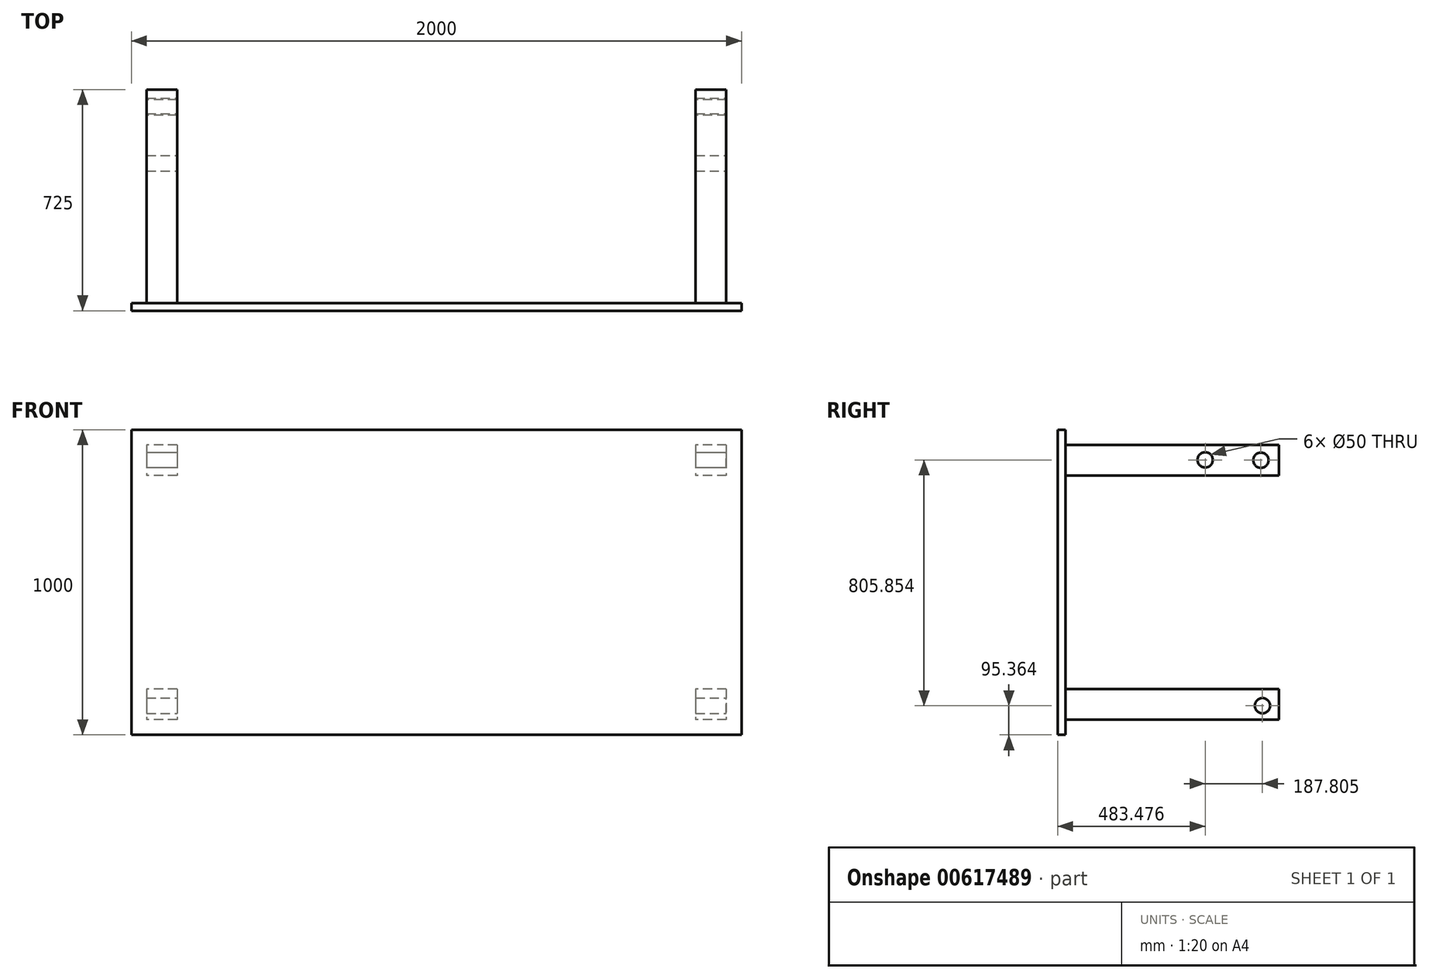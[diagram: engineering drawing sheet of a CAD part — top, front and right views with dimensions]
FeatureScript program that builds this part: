
annotation { "Feature Type Name" : "Feature", "Feature Type Description" : "" }
export const myFeature = defineFeature(function(context is Context, id is Id, definition is map)
    precondition{}
    {
        {
            var Q0;
            Q0=qCreatedBy(makeId("Front.planeOp"),FACE);
            var sketch = newSketch(context, id + "F0", { "sketchPlane" : qUnion([Q0])});
            skLineSegment(sketch, "E0.bottom", {"start": v(-997.25, 771.34) * mm, "end": v(1002.75, 771.34) * mm});
            skLineSegment(sketch, "E0.top", {"start": v(-997.25, -228.66) * mm, "end": v(1002.75, -228.66) * mm});
            skLineSegment(sketch, "E0.left", {"start": v(-997.25, 771.34) * mm, "end": v(-997.25, -228.66) * mm});
            skLineSegment(sketch, "E0.right", {"start": v(1002.75, 771.34) * mm, "end": v(1002.75, -228.66) * mm});
            skSolve(sketch);
        }
        {
            var Q0;
            Q0=makeQuery(id+"F0.imprint","IMPRINT",FACE,{"disambiguationData":[TD([[makeQuery(id+"F0.imprint","IMPRINT",EDGE,{"derivedFrom":sQuery(id+"F0.wireOp",EDGE,"E0.bottom")}),-1.0]])]});
            extrude(context, id + "F1", {"entities" : qUnion([Q0]), "depth" : 25 * mm, "offsetDistance" : 25 * mm});
        }
        {
            var Q0;
            Q0=makeQuery(id+"F1.opExtrude","CAP_FACE",FACE,{"disambiguationData":[OSD([sQuery(id+"F0.wireOp",EDGE,"E0.bottom"),sQuery(id+"F0.wireOp",EDGE,"E0.top"),sQuery(id+"F0.wireOp",EDGE,"E0.left"),sQuery(id+"F0.wireOp",EDGE,"E0.right")])],"isStart":true});
            var sketch = newSketch(context, id + "F2", { "sketchPlane" : qUnion([Q0])});
            skLineSegment(sketch, "E1.bottom", {"start": v(-952.75, 721.34) * mm, "end": v(-852.75, 721.34) * mm});
            skLineSegment(sketch, "E1.top", {"start": v(-952.75, 621.34) * mm, "end": v(-852.75, 621.34) * mm});
            skLineSegment(sketch, "E1.left", {"start": v(-952.75, 721.34) * mm, "end": v(-952.75, 621.34) * mm});
            skLineSegment(sketch, "E1.right", {"start": v(-852.75, 721.34) * mm, "end": v(-852.75, 621.34) * mm});
            skSolve(sketch);
        }
        {
            var Q0;
            Q0=makeQuery(id+"F2.imprint","IMPRINT",FACE,{"disambiguationData":[TD([[makeQuery(id+"F2.imprint","IMPRINT",EDGE,{"derivedFrom":sQuery(id+"F2.wireOp",EDGE,"E1.bottom")}),-1.0]])]});
            extrude(context, id + "F3", {"entities" : qUnion([Q0]), "operationType" : NewBodyOperationType.ADD, "depth" : 700 * mm, "offsetDistance" : 25 * mm});
        }
        {
            var Q0;
            Q0=makeQuery(id+"F1.opExtrude","CAP_FACE",FACE,{"disambiguationData":[OSD([sQuery(id+"F0.wireOp",EDGE,"E0.bottom"),sQuery(id+"F0.wireOp",EDGE,"E0.top"),sQuery(id+"F0.wireOp",EDGE,"E0.left"),sQuery(id+"F0.wireOp",EDGE,"E0.right")])],"isStart":true});
            var sketch = newSketch(context, id + "F4", { "sketchPlane" : qUnion([Q0])});
            skLineSegment(sketch, "E2.bottom", {"start": v(847.25, 721.34) * mm, "end": v(947.25, 721.34) * mm});
            skLineSegment(sketch, "E2.top", {"start": v(847.25, 621.34) * mm, "end": v(947.25, 621.34) * mm});
            skLineSegment(sketch, "E2.left", {"start": v(847.25, 721.34) * mm, "end": v(847.25, 621.34) * mm});
            skLineSegment(sketch, "E2.right", {"start": v(947.25, 721.34) * mm, "end": v(947.25, 621.34) * mm});
            skSolve(sketch);
        }
        {
            var Q0;
            Q0=makeQuery(id+"F4.imprint","IMPRINT",FACE,{"disambiguationData":[TD([[makeQuery(id+"F4.imprint","IMPRINT",EDGE,{"derivedFrom":sQuery(id+"F4.wireOp",EDGE,"E2.bottom")}),-1.0]])]});
            extrude(context, id + "F5", {"entities" : qUnion([Q0]), "operationType" : NewBodyOperationType.ADD, "depth" : 700 * mm, "offsetDistance" : 25 * mm});
        }
        {
            var Q0;
            Q0=makeQuery(id+"F1.opExtrude","CAP_FACE",FACE,{"disambiguationData":[OSD([sQuery(id+"F0.wireOp",EDGE,"E0.bottom"),sQuery(id+"F0.wireOp",EDGE,"E0.top"),sQuery(id+"F0.wireOp",EDGE,"E0.left"),sQuery(id+"F0.wireOp",EDGE,"E0.right")])],"isStart":true});
            var sketch = newSketch(context, id + "F6", { "sketchPlane" : qUnion([Q0])});
            skLineSegment(sketch, "E3.bottom", {"start": v(-952.75, -78.66) * mm, "end": v(-852.75, -78.66) * mm});
            skLineSegment(sketch, "E3.top", {"start": v(-952.75, -178.66) * mm, "end": v(-852.75, -178.66) * mm});
            skLineSegment(sketch, "E3.left", {"start": v(-952.75, -78.66) * mm, "end": v(-952.75, -178.66) * mm});
            skLineSegment(sketch, "E3.right", {"start": v(-852.75, -78.66) * mm, "end": v(-852.75, -178.66) * mm});
            skSolve(sketch);
        }
        {
            var Q0;
            Q0=makeQuery(id+"F6.imprint","IMPRINT",FACE,{"disambiguationData":[TD([[makeQuery(id+"F6.imprint","IMPRINT",EDGE,{"derivedFrom":sQuery(id+"F6.wireOp",EDGE,"E3.bottom")}),-1.0]])]});
            extrude(context, id + "F7", {"entities" : qUnion([Q0]), "operationType" : NewBodyOperationType.ADD, "depth" : 700 * mm, "offsetDistance" : 25 * mm});
        }
        {
            var Q0;
            Q0=makeQuery(id+"F1.opExtrude","CAP_FACE",FACE,{"disambiguationData":[OSD([sQuery(id+"F0.wireOp",EDGE,"E0.bottom"),sQuery(id+"F0.wireOp",EDGE,"E0.top"),sQuery(id+"F0.wireOp",EDGE,"E0.left"),sQuery(id+"F0.wireOp",EDGE,"E0.right")])],"isStart":true});
            var sketch = newSketch(context, id + "F8", { "sketchPlane" : qUnion([Q0])});
            skLineSegment(sketch, "E4.bottom", {"start": v(847.25, -78.66) * mm, "end": v(947.25, -78.66) * mm});
            skLineSegment(sketch, "E4.top", {"start": v(847.25, -178.66) * mm, "end": v(947.25, -178.66) * mm});
            skLineSegment(sketch, "E4.left", {"start": v(847.25, -78.66) * mm, "end": v(847.25, -178.66) * mm});
            skLineSegment(sketch, "E4.right", {"start": v(947.25, -78.66) * mm, "end": v(947.25, -178.66) * mm});
            skSolve(sketch);
        }
        {
            var Q0;
            Q0=makeQuery(id+"F8.imprint","IMPRINT",FACE,{"disambiguationData":[TD([[makeQuery(id+"F8.imprint","IMPRINT",EDGE,{"derivedFrom":sQuery(id+"F8.wireOp",EDGE,"E4.bottom")}),-1.0]])]});
            extrude(context, id + "F9", {"entities" : qUnion([Q0]), "operationType" : NewBodyOperationType.ADD, "depth" : 700 * mm, "offsetDistance" : 25 * mm});
        }
        {
            var Q0;
            Q0=makeQuery(id+"F5.opExtrude","SWEPT_FACE",FACE,{"disambiguationData":[OSD([sQuery(id+"F4.wireOp",EDGE,"E2.right")])]});
            var sketch = newSketch(context, id + "F10", { "sketchPlane" : qUnion([Q0])});
            skCircle(sketch, "E5", {"center": v(-641.16, 671.34) * mm, "radius": 25 * mm});
            skPoint(sketch, "E5.centerSnap0", {"position": v(-700, 671.34) * mm});
            skSolve(sketch);
        }
        {
            var Q0;
            Q0=makeQuery(id+"F10.imprint","IMPRINT",FACE,{"disambiguationData":[TD([[makeQuery(id+"F10.imprint","IMPRINT",EDGE,{"derivedFrom":sQuery(id+"F10.wireOp",EDGE,"E5")}),1.0]])]});
            var Q1;
            Q1=sQuery(id+"F10.wireOp",EDGE,"E5");
            extrude(context, id + "F11", {"entities" : qUnion([Q0]), "operationType" : NewBodyOperationType.REMOVE, "surfaceEntities" : qUnion([Q1]), "endBound" : BoundingType.THROUGH_ALL, "oppositeDirection" : true, "depth" : 100 * mm, "offsetDistance" : 25 * mm});
        }
        {
            var Q0;
            Q0=makeQuery(id+"F7.opExtrude","SWEPT_FACE",FACE,{"disambiguationData":[OSD([sQuery(id+"F6.wireOp",EDGE,"E3.left")])]});
            var sketch = newSketch(context, id + "F12", { "sketchPlane" : qUnion([Q0])});
            skCircle(sketch, "E6", {"center": v(646.28, -133.3) * mm, "radius": 25 * mm});
            skSolve(sketch);
        }
        {
            var Q0;
            Q0=makeQuery(id+"F12.imprint","IMPRINT",FACE,{"disambiguationData":[TD([[makeQuery(id+"F12.imprint","IMPRINT",EDGE,{"derivedFrom":sQuery(id+"F12.wireOp",EDGE,"E6")}),1.0]])]});
            extrude(context, id + "F13", {"entities" : qUnion([Q0]), "operationType" : NewBodyOperationType.REMOVE, "endBound" : BoundingType.THROUGH_ALL, "oppositeDirection" : true, "depth" : 25 * mm, "offsetDistance" : 25 * mm});
        }
        {
            var Q0;
            Q0=makeQuery(id+"F3.opExtrude","SWEPT_FACE",FACE,{"disambiguationData":[OSD([sQuery(id+"F2.wireOp",EDGE,"E1.left")])]});
            var sketch = newSketch(context, id + "F14", { "sketchPlane" : qUnion([Q0])});
            skCircle(sketch, "E7", {"center": v(458.48, 672.56) * mm, "radius": 25 * mm});
            skSolve(sketch);
        }
        {
            var Q0;
            Q0=makeQuery(id+"F14.imprint","IMPRINT",FACE,{"disambiguationData":[TD([[makeQuery(id+"F14.imprint","IMPRINT",EDGE,{"derivedFrom":sQuery(id+"F14.wireOp",EDGE,"E7")}),1.0]])]});
            var Q1;
            Q1=sQuery(id+"F14.wireOp",EDGE,"E7");
            extrude(context, id + "F15", {"entities" : qUnion([Q0]), "operationType" : NewBodyOperationType.REMOVE, "surfaceEntities" : qUnion([Q1]), "endBound" : BoundingType.THROUGH_ALL, "oppositeDirection" : true, "depth" : 25 * mm, "offsetDistance" : 25 * mm});
        }
    });
